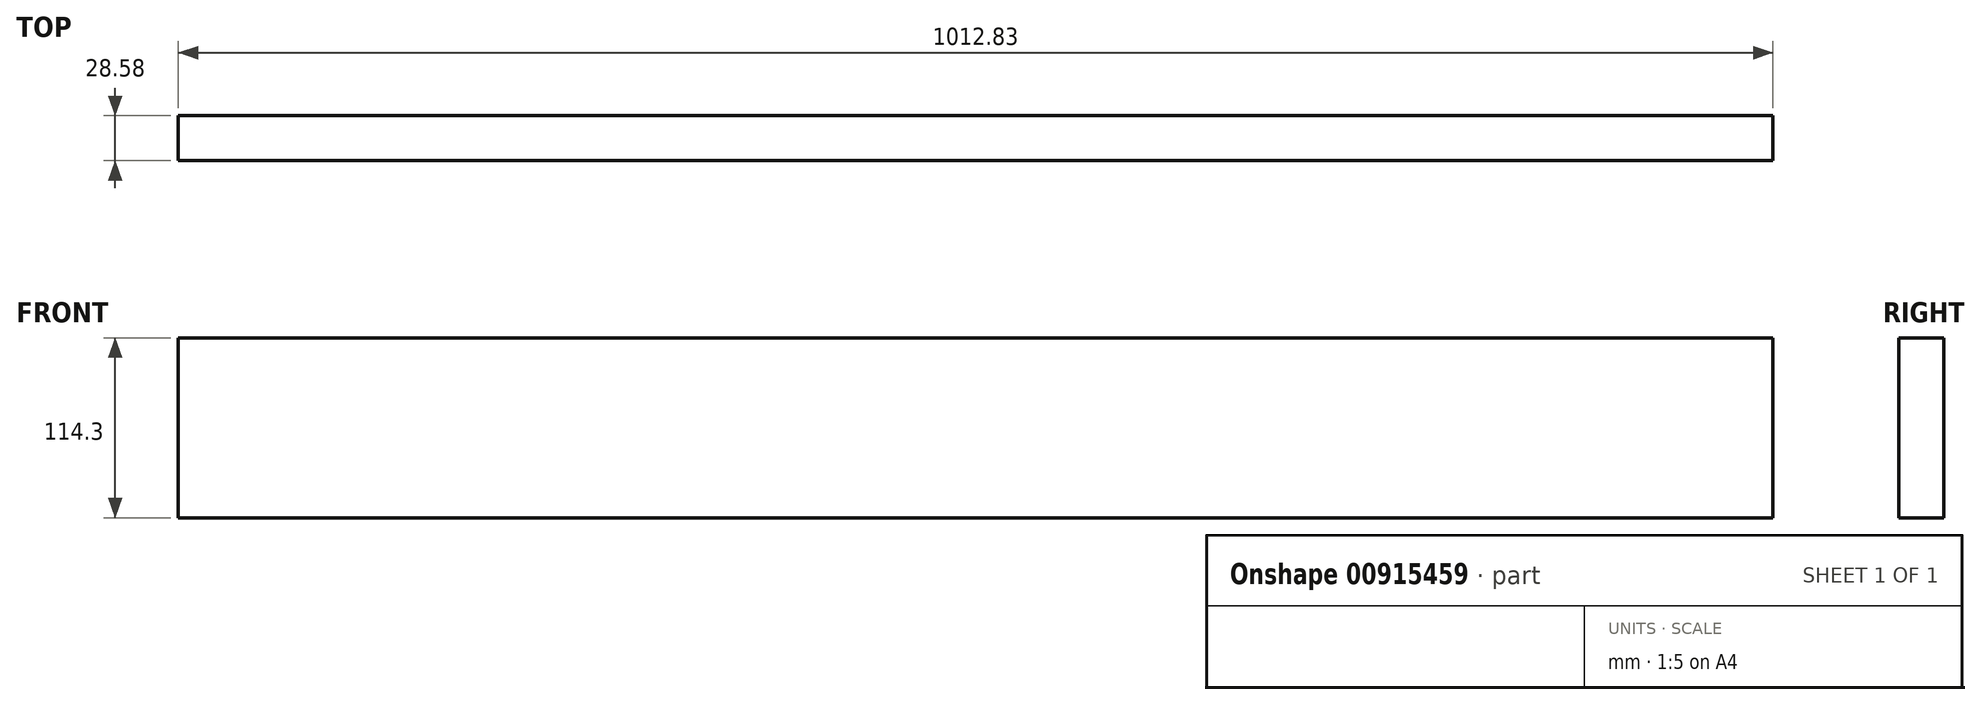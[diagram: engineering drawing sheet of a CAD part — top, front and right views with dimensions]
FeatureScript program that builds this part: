
annotation { "Feature Type Name" : "Feature", "Feature Type Description" : "" }
export const myFeature = defineFeature(function(context is Context, id is Id, definition is map)
    precondition{}
    {
        {
            var Q0;
            Q0=qCreatedBy(makeId("Right.planeOp"),FACE);
            var sketch = newSketch(context, id + "F0", { "sketchPlane" : qUnion([Q0])});
            skLineSegment(sketch, "E0.bottom", {"start": v(14.29, 57.15) * mm, "end": v(-14.29, 57.15) * mm});
            skLineSegment(sketch, "E0.top", {"start": v(14.29, -57.15) * mm, "end": v(-14.29, -57.15) * mm});
            skLineSegment(sketch, "E0.left", {"start": v(14.29, 57.15) * mm, "end": v(14.29, -57.15) * mm});
            skLineSegment(sketch, "E0.right", {"start": v(-14.29, 57.15) * mm, "end": v(-14.29, -57.15) * mm});
            skPoint(sketch, "E0.middle", {"position": v(0, 0) * mm});
            skSolve(sketch);
        }
        {
            var Q0;
            Q0=makeQuery(id+"F0.imprint","IMPRINT",FACE,{"disambiguationData":[TD([[makeQuery(id+"F0.imprint","IMPRINT",EDGE,{"derivedFrom":sQuery(id+"F0.wireOp",EDGE,"E0.bottom")}),1.0]])]});
            extrude(context, id + "F1", {"entities" : qUnion([Q0]), "depth" : 1012.82 * mm, "offsetDistance" : 25.4 * mm});
        }
    });
